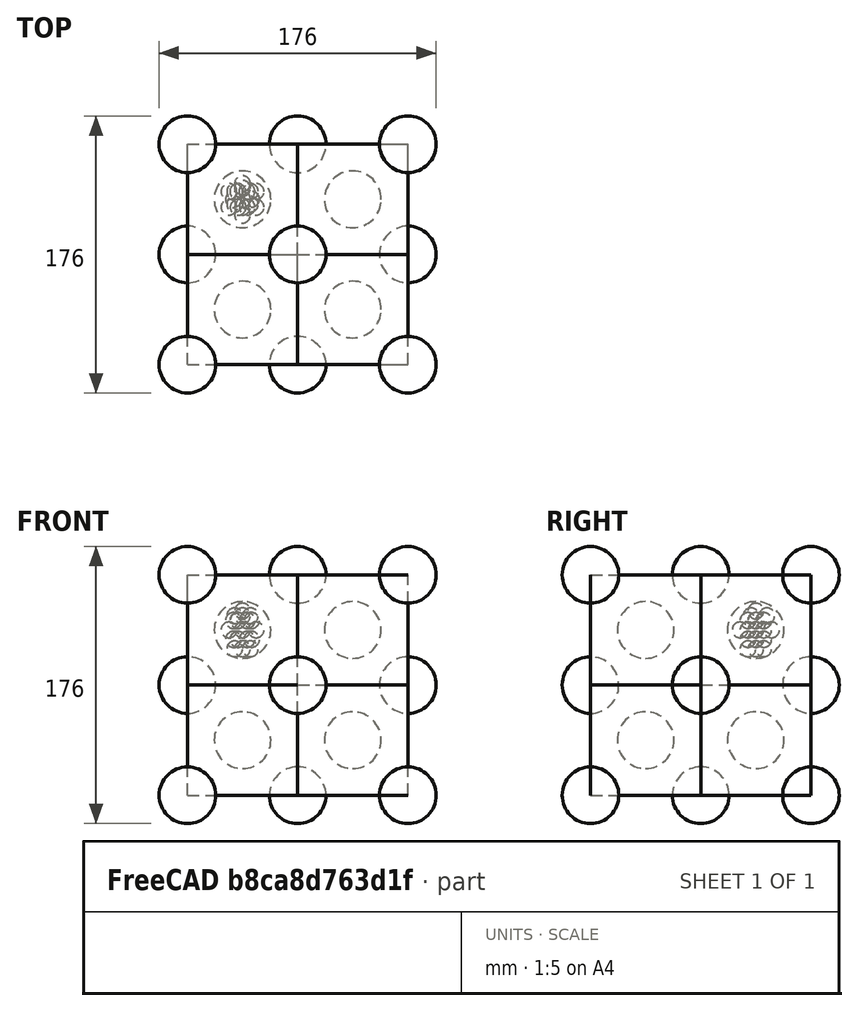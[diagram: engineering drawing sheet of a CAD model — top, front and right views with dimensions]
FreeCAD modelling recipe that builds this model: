
FCSTD DOCUMENT  (FreeCAD 1.1R43510 (Git))
Label: cristal-silicio
License: All rights reserved
LicenseURL: http://en.wikipedia.org/wiki/All_rights_reserved
objects: Part::Feature×45, Part::Sphere×10, Part::Part2DObjectPython×4, App::DocumentObjectGroup×2, Part::Box×1, Part::FeaturePython×1
note: 61 computed .brp shape members not serialized (recipe doc carries the construction recipe); baked Part::Feature solids carry a one-line shape summary decoded from their .brp

FEATURE [Part::Feature] Sphere001
  Placement = pos=(0,-10,0) rot=(0,0,1;0rad)
  shape: bbox 10 x 10 x 10 mm, 1 faces (baked)
FEATURE [Part::Feature] Sphere002
  Placement = pos=(-8.66025,-5,0) rot=(0,0,1;0rad)
  shape: bbox 10 x 10 x 10 mm, 1 faces (baked)
FEATURE [Part::Feature] Sphere003
  Placement = pos=(-8.66025,5,0) rot=(0,0,1;0rad)
  shape: bbox 10 x 10 x 10 mm, 1 faces (baked)
FEATURE [Part::Feature] Sphere004
  Placement = pos=(8.66025,-5,0) rot=(0,0,1;0rad)
  shape: bbox 10 x 10 x 10 mm, 1 faces (baked)
FEATURE [Part::Feature] Sphere005
  Placement = pos=(8.66025,5,0) rot=(0,0,1;0rad)
  shape: bbox 10 x 10 x 10 mm, 1 faces (baked)
FEATURE [Part::Feature] Sphere006
  Placement = pos=(4e-12,10,0) rot=(0,0,1;0rad)
  shape: bbox 10 x 10 x 10 mm, 1 faces (baked)
FEATURE [Part::Sphere] Sphere007  label="Center"
  Angle1 = -90
  Angle2 = 90
  Angle3 = 360
  AttacherType = Attacher::AttachEngine3D
  Radius = 5
FEATURE [Part::Feature] Sphere  label="Sphere030"
  Placement = pos=(-3,5,6) rot=(0,0,1;0rad)
  shape: bbox 10 x 10 x 10 mm, 1 faces (baked)
FEATURE [Part::Feature] Sphere008  label="Sphere031"
  Placement = pos=(2.83013,5.09808,6) rot=(0,0,1;0rad)
  shape: bbox 10 x 10 x 10 mm, 1 faces (baked)
FEATURE [Part::Feature] Sphere009  label="Sphere032"
  Placement = pos=(5.83013,0.0980762,6) rot=(0,0,1;0rad)
  shape: bbox 10 x 10 x 10 mm, 1 faces (baked)
FEATURE [Part::Feature] Sphere010  label="Sphere033"
  Placement = pos=(3,-5,6) rot=(0,0,1;0rad)
  shape: bbox 10 x 10 x 10 mm, 1 faces (baked)
FEATURE [Part::Feature] Sphere011  label="Sphere034"
  Placement = pos=(-2.83013,-5.09808,6) rot=(0,0,1;0rad)
  shape: bbox 10 x 10 x 10 mm, 1 faces (baked)
FEATURE [Part::Feature] Sphere012  label="Sphere035"
  Placement = pos=(-5.83013,-0.0980762,6) rot=(0,0,1;0rad)
  shape: bbox 10 x 10 x 10 mm, 1 faces (baked)
FEATURE [Part::Feature] Sphere013  label="Sphere036"
  Placement = pos=(-3,5,-6) rot=(0,0,1;0rad)
  shape: bbox 10 x 10 x 10 mm, 1 faces (baked)
FEATURE [Part::Feature] Sphere014  label="Sphere037"
  Placement = pos=(2.83013,5.09808,-6) rot=(0,0,1;0rad)
  shape: bbox 10 x 10 x 10 mm, 1 faces (baked)
FEATURE [Part::Feature] Sphere015  label="Sphere038"
  Placement = pos=(-2.83013,-5.09808,-6) rot=(0,0,1;0rad)
  shape: bbox 10 x 10 x 10 mm, 1 faces (baked)
FEATURE [Part::Feature] Sphere016  label="Sphere039"
  Placement = pos=(5.83013,0.0980762,-6) rot=(0,0,1;0rad)
  shape: bbox 10 x 10 x 10 mm, 1 faces (baked)
FEATURE [Part::Feature] Sphere017  label="Sphere015"
  Placement = pos=(3,-5,-6) rot=(0,0,1;0rad)
  shape: bbox 10 x 10 x 10 mm, 1 faces (baked)
FEATURE [Part::Feature] Sphere018  label="Sphere040"
  Placement = pos=(-5.83013,-0.0980762,-6) rot=(0,0,1;0rad)
  shape: bbox 10 x 10 x 10 mm, 1 faces (baked)
FEATURE [Part::Sphere] Sphere019
  Angle1 = -90
  Angle2 = 90
  Angle3 = 360
  AttacherType = Attacher::AttachEngine3D
  Placement = pos=(0,0,12) rot=(0,0,1;0rad)
  Radius = 5
FEATURE [Part::Sphere] Sphere020  label="Sphere041"
  Angle1 = -90
  Angle2 = 90
  Angle3 = 360
  AttacherType = Attacher::AttachEngine3D
  Placement = pos=(0,0,-12) rot=(0,0,1;0rad)
  Radius = 5
FEATURE [Part::Sphere] Sphere021  label="Sphere042"
  Angle1 = -90
  Angle2 = 90
  Angle3 = 360
  AttacherType = Attacher::AttachEngine3D
  Placement = pos=(0,7,9) rot=(0,0,1;0rad)
  Radius = 5
FEATURE [Part::Sphere] Sphere022  label="Sphere043"
  Angle1 = -90
  Angle2 = 90
  Angle3 = 360
  AttacherType = Attacher::AttachEngine3D
  Placement = pos=(-5,-3,9) rot=(0,0,1;0rad)
  Radius = 5
FEATURE [Part::Sphere] Sphere023  label="Sphere044"
  Angle1 = -90
  Angle2 = 90
  Angle3 = 360
  AttacherType = Attacher::AttachEngine3D
  Placement = pos=(5,-3,9) rot=(0,0,1;0rad)
  Radius = 5
FEATURE [Part::Sphere] Sphere024  label="Sphere045"
  Angle1 = -90
  Angle2 = 90
  Angle3 = 360
  AttacherType = Attacher::AttachEngine3D
  Placement = pos=(-5,5,-12) rot=(0,0,1;0rad)
  Radius = 5
FEATURE [Part::Sphere] Sphere025  label="Sphere046"
  Angle1 = -90
  Angle2 = 90
  Angle3 = 360
  AttacherType = Attacher::AttachEngine3D
  Placement = pos=(5,5,-12) rot=(0,0,1;0rad)
  Radius = 5
FEATURE [Part::Sphere] Sphere026  label="Sphere047"
  Angle1 = -90
  Angle2 = 90
  Angle3 = 360
  AttacherType = Attacher::AttachEngine3D
  Placement = pos=(0,-5,-12) rot=(0,0,1;0rad)
  Radius = 5
FEATURE [App::DocumentObjectGroup] Group  label="core"
  Group = -> [Sphere001,Sphere002,Sphere003,Sphere004,Sphere005,Sphere006,Sphere007,Sphere,Sphere008,Sphere009,Sphere010,Sphere011,Sphere012,Sphere013,Sphere014,Sphere015,Sphere016,Sphere017,Sphere018,Sphere019,Sphere020,Sphere021,Sphere022,Sphere023,Sphere024,Sphere025,Sphere026]
FEATURE [Part::Part2DObjectPython] Polygon  # Draft 2D object (typed FeaturePython)
  ChamferSize = 0
  DrawMode = 0
  FacesNumber = 3
  FilletRadius = 0
  MakeFace = false
  MapMode = 5
  Placement = pos=(0,0,-31) rot=(0,0,1;0rad)
  Radius = 50
FEATURE [Part::Part2DObjectPython] Line002  # Draft 2D object (typed FeaturePython)
  ChamferSize = 0
  Closed = false
  End = (-25,-43.3013,-31)
  FilletRadius = 0
  Length = 87.0816
  MakeFace = true
  MapMode = 5
  Placement = pos=(0,0,-31) rot=(0,0,1;0rad)
  Points = (2) [(1.07885,0,70.9091),(-25,-43.3013,0)]
  Start = (1.07885,0,39.9091)
  Subdivisions = 0
FEATURE [Part::Part2DObjectPython] Line003  # Draft 2D object (typed FeaturePython)
  ChamferSize = 0
  Closed = false
  End = (50,0,-31)
  FilletRadius = 0
  Length = 86.1474
  MakeFace = true
  MapMode = 5
  Placement = pos=(0,0,-31) rot=(0,0,1;0rad)
  Points = (2) [(1.07885,0,70.9091),(50,1.53081e-15,0)]
  Start = (1.07885,0,39.9091)
  Subdivisions = 0
FEATURE [Part::Part2DObjectPython] Line004  # Draft 2D object (typed FeaturePython)
  ChamferSize = 0
  Closed = false
  End = (-25,43.3013,-31)
  FilletRadius = 0
  Length = 87.0816
  MakeFace = true
  MapMode = 5
  Placement = pos=(0,0,-31) rot=(0,0,1;0rad)
  Points = (2) [(1.07885,0,70.9091),(-25,43.3013,0)]
  Start = (1.07885,0,39.9091)
  Subdivisions = 0
FEATURE [App::DocumentObjectGroup] Group001  label="tetrahedron"
  Group = -> [Line002,Line003,Line004,Polygon]
FEATURE [Part::Box] Box  label="Cube"
  AttacherType = Attacher::AttachEngine3D
  Height = 70
  Length = 70
  Placement = pos=(-35,-35,-35) rot=(0,0,1;0rad)
  Width = 70
FEATURE [Part::Sphere] Sphere027  label="Sphere"
  Angle1 = -90
  Angle2 = 90
  Angle3 = 360
  AttacherType = Attacher::AttachEngine3D
  Radius = 18
FEATURE [Part::FeaturePython] Clone  label="Clone of Sphere"  # Draft clone (typed FeaturePython)
  ForceCompound = false
  Fuse = false
  Objects = -> [Sphere027]
  Placement = pos=(-35,35,35) rot=(0,0,1;0rad)
  Scale = (1,1,1)
FEATURE [Part::Feature] Clone001  label="Clone of Sphere001"
  Placement = pos=(-35,-35,-35) rot=(0,0,1;0rad)
  shape: bbox 36 x 36 x 36 mm, 1 faces (baked)
FEATURE [Part::Feature] Clone002  label="Clone of Sphere002"
  Placement = pos=(35,-35,35) rot=(0,0,1;0rad)
  shape: bbox 36 x 36 x 36 mm, 1 faces (baked)
FEATURE [Part::Feature] Clone003  label="Clone of Sphere003"
  Placement = pos=(35,35,-35) rot=(0,0,1;0rad)
  shape: bbox 36 x 36 x 36 mm, 1 faces (baked)
FEATURE [Part::Feature] Clone004  label="Clone of Sphere004"
  Placement = pos=(35,-35,-105) rot=(0,0,1;0rad)
  shape: bbox 36 x 36 x 36 mm, 1 faces (baked)
FEATURE [Part::Feature] Sphere028  label="Sphere048"
  Placement = pos=(70,0,-70) rot=(0,0,1;0rad)
  shape: bbox 36 x 36 x 36 mm, 1 faces (baked)
FEATURE [Part::Feature] Clone005  label="Clone of Sphere005"
  Placement = pos=(105,-35,-35) rot=(0,0,1;0rad)
  shape: bbox 36 x 36 x 36 mm, 1 faces (baked)
FEATURE [Part::Feature] Clone006  label="Clone of Sphere006"
  Placement = pos=(105,35,-105) rot=(0,0,1;0rad)
  shape: bbox 36 x 36 x 36 mm, 1 faces (baked)
FEATURE [Part::Feature] Box001  label="Cube001"
  Placement = pos=(35,-35,-105) rot=(0,0,1;0rad)
  shape: bbox 70 x 70 x 70 mm, 6 faces (baked)
FEATURE [Part::Feature] Clone007  label="Clone of Sphere007"
  Placement = pos=(-35,-105,-105) rot=(0,0,1;0rad)
  shape: bbox 36 x 36 x 36 mm, 1 faces (baked)
FEATURE [Part::Feature] Clone008  label="Clone of Sphere008"
  Placement = pos=(35,-105,-35) rot=(0,0,1;0rad)
  shape: bbox 36 x 36 x 36 mm, 1 faces (baked)
FEATURE [Part::Feature] Sphere029  label="Sphere049"
  Placement = pos=(0,-70,-70) rot=(0,0,1;0rad)
  shape: bbox 36 x 36 x 36 mm, 1 faces (baked)
FEATURE [Part::Feature] Box002  label="Cube002"
  Placement = pos=(-35,-105,-105) rot=(0,0,1;0rad)
  shape: bbox 70 x 70 x 70 mm, 6 faces (baked)
FEATURE [Part::Feature] Sphere030  label="Sphere050"
  Placement = pos=(0,-70,0) rot=(0,0,1;0rad)
  shape: bbox 36 x 36 x 36 mm, 1 faces (baked)
FEATURE [Part::Feature] Box003  label="Cube003"
  Placement = pos=(-35,-105,-35) rot=(0,0,1;0rad)
  shape: bbox 70 x 70 x 70 mm, 6 faces (baked)
FEATURE [Part::Feature] Clone009  label="Clone of Sphere009"
  Placement = pos=(-35,-105,35) rot=(0,0,1;0rad)
  shape: bbox 36 x 36 x 36 mm, 1 faces (baked)
FEATURE [Part::Feature] Sphere031  label="Sphere051"
  Placement = pos=(70,0,0) rot=(0,0,1;0rad)
  shape: bbox 36 x 36 x 36 mm, 1 faces (baked)
FEATURE [Part::Feature] Box004  label="Cube004"
  Placement = pos=(35,-35,-35) rot=(0,0,1;0rad)
  shape: bbox 70 x 70 x 70 mm, 6 faces (baked)
FEATURE [Part::Feature] Clone012  label="Clone of Sphere012"
  Placement = pos=(105,35,35) rot=(0,0,1;0rad)
  shape: bbox 36 x 36 x 36 mm, 1 faces (baked)
FEATURE [Part::Feature] Box005  label="Cube005"
  Placement = pos=(35,-105,-105) rot=(0,0,1;0rad)
  shape: bbox 70 x 70 x 70 mm, 6 faces (baked)
FEATURE [Part::Feature] Clone013  label="Clone of Sphere013"
  Placement = pos=(105,-105,-105) rot=(0,0,1;0rad)
  shape: bbox 36 x 36 x 36 mm, 1 faces (baked)
FEATURE [Part::Feature] Box006  label="Cube006"
  Placement = pos=(35,-105,-35) rot=(0,0,1;0rad)
  shape: bbox 70 x 70 x 70 mm, 6 faces (baked)
FEATURE [Part::Feature] Clone014  label="Clone of Sphere014"
  Placement = pos=(105,-105,35) rot=(0,0,1;0rad)
  shape: bbox 36 x 36 x 36 mm, 1 faces (baked)
FEATURE [Part::Feature] Sphere032  label="Sphere052"
  Placement = pos=(70,-70,-70) rot=(0,0,1;0rad)
  shape: bbox 36 x 36 x 36 mm, 1 faces (baked)
FEATURE [Part::Feature] Box007  label="Cube007"
  Placement = pos=(-35,-35,-105) rot=(0,0,1;0rad)
  shape: bbox 70 x 70 x 70 mm, 6 faces (baked)
FEATURE [Part::Feature] Clone015  label="Clone of Sphere015"
  Placement = pos=(-35,35,-105) rot=(0,0,1;0rad)
  shape: bbox 36 x 36 x 36 mm, 1 faces (baked)
FEATURE [Part::Feature] Sphere033  label="Sphere053"
  Placement = pos=(0,0,-70) rot=(0,0,1;0rad)
  shape: bbox 36 x 36 x 36 mm, 1 faces (baked)
FEATURE [Part::Feature] Sphere034  label="Sphere054"
  Placement = pos=(70,-70,0) rot=(0,0,1;0rad)
  shape: bbox 36 x 36 x 36 mm, 1 faces (baked)
